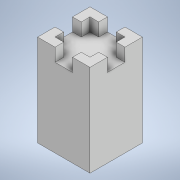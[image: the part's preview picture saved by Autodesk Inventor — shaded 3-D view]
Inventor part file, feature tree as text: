
AUTODESK INVENTOR PART (.ipt)
format: ipt  version: 2021 (Build 250183000, 183)  size: 130,048 bytes
history: native  units: in
note: dims shown in document units (in); Inventor stores cm internally (conversion verified against a paired STEP export)
features: extrude x2, sketch x2, projected_geometry x1
ambient origin geometry x8: Origin, YZ Plane, XZ Plane, XY Plane, X Axis, Y Axis, Z Axis, Center Point
bodies: Solid1 (feature_tree)
feature tree (5):
  extrude  "Extrusion1"  Depth=0.7874in
  extrude  "Extrusion2"  Depth=0.2622in
  sketch  "Sketch1"  dims[d0=0.7874in d1=0.7874in]
  sketch  "Sketch2"  dims[d2=1.1811in d3=0.0in d4=0.2622in d5=0.1311in d6=0.1311in d7=0.1311in d8=0.1969in d9=0.0in]
  projected_geometry  "Projected Loop1"
